# Revit family: P500276-031-30
name_source: partatom
category: Lighting Fixtures
revit_build: Autodesk Revit 2014 (Build: 20130308_1515(x64)
units: mm (PartAtom-declared; Revit-internal decimal feet)

## types (1)
- P500276-031-30
    Apparent Load = 39 VA
    Assembly Code = D5020200
    BLUE = Paint- Hubbell - Blue
    Color Filter = 16777215
    Connector Description = Lighting Connector
    Default Elevation = 48"
    Depth = 1 3/4"
    Description = Provide a dramatic architectural lighting design to any space with this LED pendant. A smooth metal beam with a black finish suspends from the ceiling to add clean visual interest to minimalist residential or commercial settings. The frame holds a polycarbonate shade in place to complete the design.
    Dimming Lamp Color Temperature Shift = <None>
    Fixture distribution = Direct
    Glass = Hubbell - Glass
    Gold = Hubbell - Gold
    Height = 1 3/8"
    Housing Material = Paint - Hubbell - Textured Camera Black
    Lamp = LED
    Load Classification = Lighting
    Manufacturer = Progress Lighting
    Model = P500276-031-30
    Photometric Web File = generic
    Power Factor = 1
    Product Documentation Link = https://hubbellcdn.com
    Product Link = https://www.hubbell.com
    Specifications = The frame holds a polycarbonate shade in place to complete the design.
A smooth metal beam with a black finish suspends from the ceiling to add clean visual interest to minimalist residential or commercial settings.
Provide a dramatic architectural lighting design to any space.
Ideal for any hallway, foyer, kitchen, or dining room.
Perfect for transitional, modern, or contemporary settings.
Measures 47-1/4-inch width by 1-3/8-inch height.
Uses one integrated LED that is included (39w max).
Compatible with many Triac/ELV dimmers (see dimming controls)
Includes installation instructions and mounting hardware.
Progress Lighting products are designed for exceptional quality, reliability, and functionality.
    Tilt Angle = 60.00°
    URL = https://www.hubbell.com
    Voltage = 120 V
    Warranty = 5 years Warranty
    Wattage Comments = 39 W
    Watts = 39 W
    White = Paint - Hubbell - Matte White
    Width = 47 1/4"

## geometry (parser evidence)
native form markers: Sweep x3
no freeform markers — native parametric forms only
